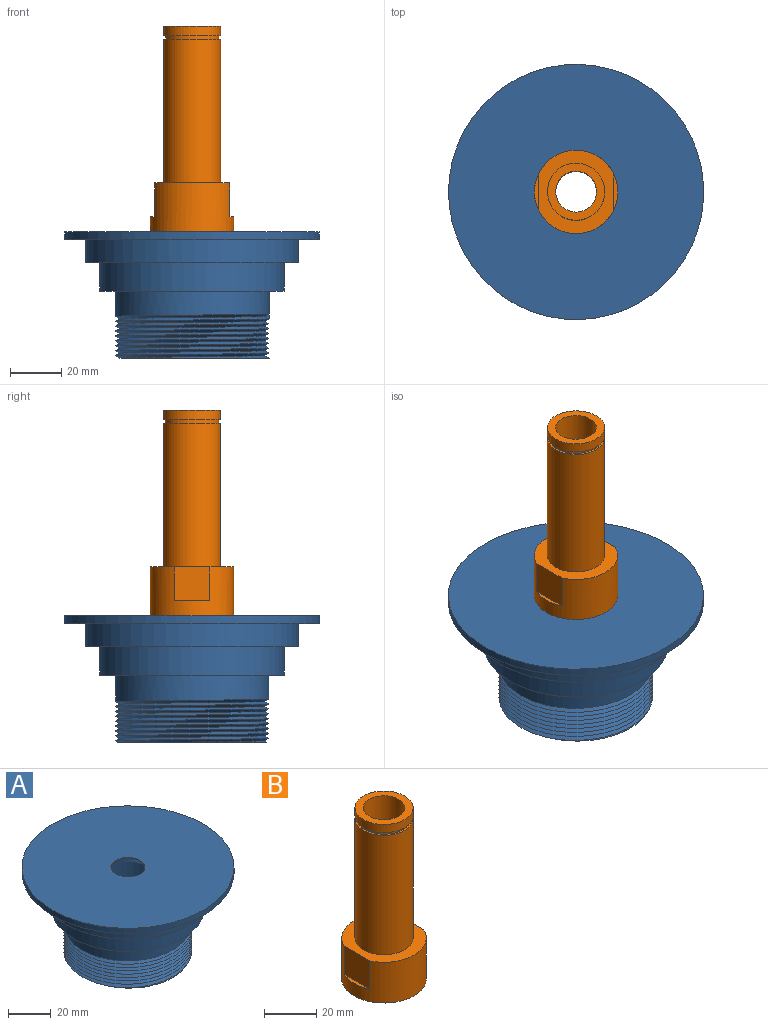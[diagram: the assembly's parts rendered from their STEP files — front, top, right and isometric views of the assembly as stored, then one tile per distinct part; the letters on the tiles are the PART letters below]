
ASSEMBLY  parts=2 mates=1
PART A: 52 faces, bbox 100.8x100.8x51.9 mm
  f0: cylinder r=29.91mm len=29.92mm, axis (0,0,1), area 0.1mm2, adj f20,f23,f46,f48
  f1: cylinder r=29.91mm len=59.82mm, axis (0,0,1), area 0.5mm2, adj f22,f23,f44,f47
  f2: cylinder r=29.91mm len=59.82mm, axis (0,0,1), area 0.5mm2, adj f22,f23,f42,f45
  f3: cylinder r=29.91mm len=59.82mm, axis (0,0,1), area 0.5mm2, adj f22,f23,f40,f43
  f4: cylinder r=29.91mm len=59.82mm, axis (0,0,1), area 0.5mm2, adj f22,f23,f38,f41
  f5: cylinder r=29.91mm len=59.82mm, axis (0,0,1), area 0.5mm2, adj f22,f23,f36,f39
  f6: cylinder r=29.91mm len=59.82mm, axis (0,0,1), area 0.5mm2, adj f22,f23,f34,f37
  f7: cylinder r=29.91mm len=59.82mm, axis (0,0,1), area 0.5mm2, adj f22,f23,f32,f35
  f8: cylinder r=29.91mm len=59.82mm, axis (0,0,1), area 1808.1mm2, adj f9,f18,f22,f23,f24,f33,f49,f51
  f9: cylinder r=29.91mm len=59.82mm, axis (0,0,1), area 0.4mm2, adj f8,f22,f33,f50
  f10: cylinder r=23.3mm len=46.61mm, axis (0,0,1), area 5225.5mm2, adj f26,f29
  f11: cylinder r=49.59mm len=99.19mm, axis (0,0,1), area 949.8mm2, adj f13,f14
  f12: cylinder r=7.94mm len=15.88mm, axis (0,0,1), area 31.7mm2, adj f14,f31
  f13: plane 99.19x99.19mm, normal (0,0,-1), area 2358.2mm2, adj f11,f15
  f14: plane 99.19x99.19mm, normal (0,0,1), area 7528.9mm2, adj f11,f12
  f15: cylinder r=41.34mm len=82.68mm, axis (0,0,1), area 2342.1mm2, adj f13,f16
  f16: plane 82.68x82.68mm, normal (0,0,-1), area 1324.7mm2, adj f15,f17
  f17: cylinder r=35.88mm len=71.76mm, axis (0,0,1), area 2462.1mm2, adj f16,f18
  f18: plane 71.76x71.76mm, normal (0,0,-1), area 1233.6mm2, adj f8,f17
  f19: cylinder r=23.3mm len=46.61mm, axis (0,0,1), area 502.1mm2, adj f20,f27
  f20: plane 59.76x59.57mm, normal (0,0,-1), area 941.4mm2, adj f0,f19,f21,f22,f23,f46,f47,f48
  f21: plane 21.82x7.87mm, normal (0,1,0), area 165.1mm2, adj f20,f22,f23,f24
  f22: plane 17.89x2.03mm, normal (1,0,0), area 23.3mm2, adj f1,f2,f3,f4,f5,f6,f7,f8
  f23: plane 17.89x2.03mm, normal (-1,0,0), area 23.4mm2, adj f0,f1,f2,f3,f4,f5,f6,f7
  f24: cylinder r=3.94mm len=7.87mm, axis (0,-1,0), area 25.1mm2, adj f8,f21,f22,f23
  f25: cylinder r=24.32mm len=48.64mm, axis (0,0,-1), area 291.1mm2, adj f26,f27
  f26: plane 48.64x48.64mm, normal (0,0,-1), area 152mm2, adj f10,f25
  f27: plane 48.64x48.64mm, normal (0,0,1), area 152mm2, adj f19,f25
  f28: cylinder r=19.49mm len=38.99mm, axis (0,0,1), area 108.9mm2, adj f29,f30
  f29: plane 46.61x46.61mm, normal (0,0,-1), area 512.3mm2, adj f10,f28
  f30: plane 38.99x38.99mm, normal (0,0,-1), area 541.2mm2, adj f28,f31
  f31: cone r=14.41mm half-angle=45deg, axis (0,0,-1), area 643.2mm2, adj f12,f30
  f32: bspline ~69.07x59.82mm, area 332.7mm2, adj f7,f22,f23,f33
  f33: bspline ~69.07x59.82mm, area 332.7mm2, adj f8,f9,f22,f23,f32
  f34: bspline ~69.07x59.82mm, area 332.7mm2, adj f6,f22,f23,f35
  f35: bspline ~69.07x59.82mm, area 332.7mm2, adj f7,f22,f23,f34
  f36: bspline ~69.07x59.82mm, area 332.7mm2, adj f5,f22,f23,f37
  f37: bspline ~69.07x59.82mm, area 332.7mm2, adj f6,f22,f23,f36
  f38: bspline ~69.07x59.82mm, area 332.7mm2, adj f4,f22,f23,f39
  f39: bspline ~69.07x59.82mm, area 332.7mm2, adj f5,f22,f23,f38
  f40: bspline ~69.07x59.82mm, area 332.7mm2, adj f3,f22,f23,f41
  f41: bspline ~69.07x59.82mm, area 332.7mm2, adj f4,f22,f23,f40
  f42: bspline ~69.07x59.82mm, area 332.7mm2, adj f2,f22,f23,f43
  f43: bspline ~69.07x59.82mm, area 332.7mm2, adj f3,f22,f23,f42
  f44: bspline ~69.07x59.82mm, area 332.7mm2, adj f1,f22,f23,f45
  f45: bspline ~69.07x59.82mm, area 332.7mm2, adj f2,f22,f23,f44
  f46: bspline ~69.07x59.82mm, area 165.9mm2, adj f0,f20,f23,f47
  f47: bspline ~69.07x59.82mm, area 315.2mm2, adj f1,f20,f22,f23,f46
  f48: bspline ~44.86x34.54mm, area 18.5mm2, adj f0,f20,f23
  f49: bspline ~69.07x59.82mm, area 253.3mm2, adj f8,f22,f50,f51
  f50: bspline ~69.07x59.82mm, area 253.3mm2, adj f9,f22,f49,f51
  f51: plane 1.9x1.65mm, normal (0,-1,0), area 1.6mm2, adj f8,f49,f50
PART B: 14 faces, bbox 32.4x32.4x80 mm
  f0: cylinder r=11.11mm len=55.88mm, axis (0,0,-1), area 3901.6mm2, adj f8,f12
  f1: cylinder r=7.94mm len=80.01mm, axis (0,0,-1), area 3990.3mm2, adj f3,f4
  f2: cylinder r=11.11mm len=22.23mm, axis (0,0,-1), area 266mm2, adj f3,f13
  f3: plane 22.23x22.23mm, normal (0,0,1), area 190mm2, adj f1,f2
  f4: plane 32.39x32.39mm, normal (0,0,-1), area 625.8mm2, adj f1,f6
  f5: plane 13.97x13.21mm, normal (1,0,0), area 184.5mm2, adj f6,f8,f10
  f6: cylinder r=16.19mm len=32.39mm, axis (0,0,-1), area 1556.6mm2, adj f4,f5,f7,f8,f9,f10
  f7: plane 13.97x13.21mm, normal (-1,0,0), area 184.5mm2, adj f6,f8,f9
  f8: plane 32.39x29.22mm, normal (0,0,1), area 406mm2, adj f0,f5,f6,f7
  f9: plane 13.97x1.58mm, normal (0,0,1), area 14.9mm2, adj f6,f7
  f10: plane 13.97x1.58mm, normal (0,0,1), area 14.9mm2, adj f5,f6
  f11: cylinder r=10.35mm len=20.7mm, axis (0,0,1), area 82.6mm2, adj f12,f13
  f12: plane 22.23x22.23mm, normal (0,0,1), area 51.4mm2, adj f0,f11
  f13: plane 22.23x22.23mm, normal (0,0,-1), area 51.4mm2, adj f2,f11
PLACE A t=(-2.44,-16.59,6.94)mm
PLACE B t=(-2.44,-16.59,6.94)mm
MATE fastened A.f12 <-> B.f1  axis (0,0,1) through (-2.44,-16.59,6.94)mm
